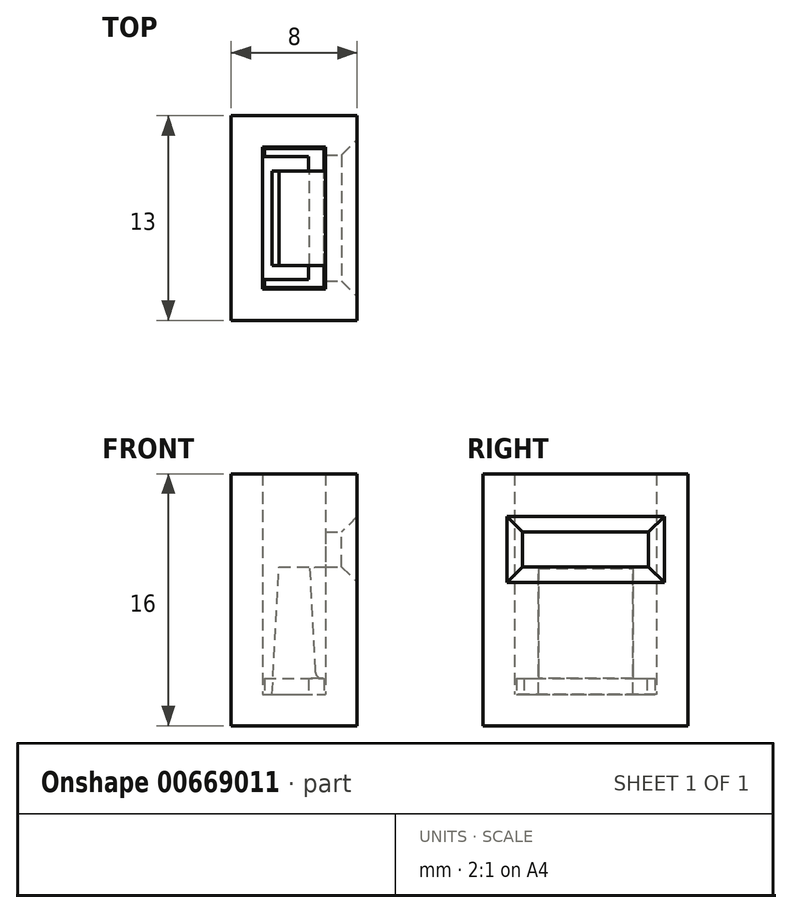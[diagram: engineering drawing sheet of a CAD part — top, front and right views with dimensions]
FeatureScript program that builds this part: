
annotation { "Feature Type Name" : "Feature", "Feature Type Description" : "" }
export const myFeature = defineFeature(function(context is Context, id is Id, definition is map)
    precondition{}
    {
        {
            var Q0;
            Q0=qCreatedBy(makeId("Top.planeOp"),FACE);
            var sketch = newSketch(context, id + "F0", { "sketchPlane" : qUnion([Q0])});
            skLineSegment(sketch, "E0.bottom", {"start": v(-2, 4.5) * mm, "end": v(2, 4.5) * mm});
            skLineSegment(sketch, "E0.top", {"start": v(-2, -4.5) * mm, "end": v(2, -4.5) * mm});
            skLineSegment(sketch, "E0.left", {"start": v(-2, 4.5) * mm, "end": v(-2, -4.5) * mm});
            skLineSegment(sketch, "E0.right", {"start": v(2, 4.5) * mm, "end": v(2, -4.5) * mm});
            skLineSegment(sketch, "E1.bottom", {"start": v(-4, 6.5) * mm, "end": v(4, 6.5) * mm});
            skLineSegment(sketch, "E1.top", {"start": v(-4, -6.5) * mm, "end": v(4, -6.5) * mm});
            skLineSegment(sketch, "E1.left", {"start": v(-4, 6.5) * mm, "end": v(-4, -6.5) * mm});
            skLineSegment(sketch, "E1.right", {"start": v(4, 6.5) * mm, "end": v(4, -6.5) * mm});
            skLineSegment(sketch, "E2", {"start": v(0, 4.5) * mm, "end": v(0, -4.5) * mm});
            skLineSegment(sketch, "E3", {"start": v(-2, 0) * mm, "end": v(2, 0) * mm});
            skSolve(sketch);
        }
        {
            var Q0;
            Q0=makeQuery(id+"F0.imprint","IMPRINT",FACE,{"disambiguationData":[TD([[makeQuery(id+"F0.imprint","IMPRINT",EDGE,{"derivedFrom":sQuery(id+"F0.wireOp",EDGE,"E1.bottom")}),-1.0]])]});
            extrude(context, id + "F1", {"entities" : qUnion([Q0]), "depth" : 14 * mm, "offsetDistance" : 25 * mm});
        }
        {
            var Q0;
            Q0=qCreatedBy(makeId("Front.planeOp"),FACE);
            var sketch = newSketch(context, id + "F2", { "sketchPlane" : qUnion([Q0])});
            skLineSegment(sketch, "E4", {"start": v(-1.4, 0) * mm, "end": v(1.4, 0) * mm});
            skLineSegment(sketch, "E5", {"start": v(-1.4, 0) * mm, "end": v(-0.88, 10) * mm});
            skLineSegment(sketch, "E6", {"start": v(-0.88, 10) * mm, "end": v(2.03, 10) * mm});
            skLineSegment(sketch, "E7", {"start": v(2.4, 8.62) * mm, "end": v(2.03, 10) * mm});
            skLineSegment(sketch, "E8", {"start": v(2.4, 8.62) * mm, "end": v(2.4, 8.12) * mm});
            skLineSegment(sketch, "E9", {"start": v(2.4, 8.12) * mm, "end": v(0.98, 8) * mm});
            skLineSegment(sketch, "E10", {"start": v(0.98, 8) * mm, "end": v(1.4, 0) * mm});
            skLineSegment(sketch, "E11", {"start": v(-1.4, 0) * mm, "end": v(-1.4, 10) * mm});
            skLineSegment(sketch, "E12", {"start": v(-1.4, 10) * mm, "end": v(-0.88, 10) * mm});
            skLineSegment(sketch, "E13", {"start": v(2.4, 8.12) * mm, "end": v(2.4, 0) * mm});
            skLineSegment(sketch, "E14", {"start": v(2.4, 0) * mm, "end": v(1.4, 0) * mm});
            skLineSegment(sketch, "E15", {"start": v(2.03, 10) * mm, "end": v(2.4, 10) * mm});
            skLineSegment(sketch, "E16", {"start": v(2.4, 10) * mm, "end": v(2.4, 8.62) * mm});
            skLineSegment(sketch, "E17.0", {"start": v(2, 14) * mm, "end": v(2, 0) * mm});
            skLineSegment(sketch, "E18.0", {"start": v(-2, 14) * mm, "end": v(-2, 0) * mm});
            skLineSegment(sketch, "E19.bottom", {"start": v(-1.5, 10.3) * mm, "end": v(5.4, 10.3) * mm});
            skLineSegment(sketch, "E19.top", {"start": v(-1.5, 8.1) * mm, "end": v(5.4, 8.1) * mm});
            skLineSegment(sketch, "E19.left", {"start": v(-1.5, 10.3) * mm, "end": v(-1.5, 8.1) * mm});
            skLineSegment(sketch, "E19.right", {"start": v(5.4, 10.3) * mm, "end": v(5.4, 8.1) * mm});
            skSolve(sketch);
        }
        {
            var Q0;
            Q0=makeQuery(id+"F1.opExtrude","CAP_FACE",FACE,{"disambiguationData":[OSD([sQuery(id+"F0.wireOp",EDGE,"E0.bottom"),sQuery(id+"F0.wireOp",EDGE,"E0.top"),sQuery(id+"F0.wireOp",EDGE,"E0.left"),sQuery(id+"F0.wireOp",EDGE,"E0.right"),sQuery(id+"F0.wireOp",EDGE,"E1.bottom"),sQuery(id+"F0.wireOp",EDGE,"E1.top"),sQuery(id+"F0.wireOp",EDGE,"E1.left"),sQuery(id+"F0.wireOp",EDGE,"E1.right")])],"isStart":true});
            var sketch = newSketch(context, id + "F3", { "sketchPlane" : qUnion([Q0])});
            skLineSegment(sketch, "E20.bottom", {"start": v(-1.9, 4.4) * mm, "end": v(1.9, 4.4) * mm});
            skLineSegment(sketch, "E20.top", {"start": v(-1.9, -4.4) * mm, "end": v(1.9, -4.4) * mm});
            skLineSegment(sketch, "E20.left", {"start": v(-1.9, 4.4) * mm, "end": v(-1.9, -4.4) * mm});
            skLineSegment(sketch, "E20.right", {"start": v(1.9, 4.4) * mm, "end": v(1.9, -4.4) * mm});
            skLineSegment(sketch, "E21.bottom", {"start": v(-4, 6.5) * mm, "end": v(4, 6.5) * mm});
            skLineSegment(sketch, "E21.top", {"start": v(-4, -6.5) * mm, "end": v(4, -6.5) * mm});
            skLineSegment(sketch, "E21.left", {"start": v(-4, 6.5) * mm, "end": v(-4, -6.5) * mm});
            skLineSegment(sketch, "E21.right", {"start": v(4, 6.5) * mm, "end": v(4, -6.5) * mm});
            skLineSegment(sketch, "E22.bottom", {"start": v(-1.9, 3.9) * mm, "end": v(0.9, 3.9) * mm});
            skLineSegment(sketch, "E22.top", {"start": v(-1.9, -3.9) * mm, "end": v(0.9, -3.9) * mm});
            skLineSegment(sketch, "E22.left", {"start": v(-1.9, 3.9) * mm, "end": v(-1.9, -3.9) * mm});
            skLineSegment(sketch, "E22.right", {"start": v(0.9, 3.9) * mm, "end": v(0.9, -3.9) * mm});
            skSolve(sketch);
        }
        {
            var Q0;
            Q0=makeQuery(id+"F3.imprint","IMPRINT",FACE,{"disambiguationData":[TD([[makeQuery(id+"F3.imprint","IMPRINT",EDGE,{"derivedFrom":sQuery(id+"F3.wireOp",EDGE,"E21.bottom")}),-1.0]])]});
            var Q1;
            Q1=makeQuery(id+"F3.imprint","IMPRINT",FACE,{"disambiguationData":[TD([[makeQuery(id+"F3.imprint","IMPRINT",EDGE,{"derivedFrom":sQuery(id+"F3.wireOp",EDGE,"E20.bottom")}),-1.0]])]});
            var Q2;
            Q2=makeQuery(id+"F3.imprint","IMPRINT",FACE,{"disambiguationData":[TD([[makeQuery(id+"F3.imprint","IMPRINT",EDGE,{"derivedFrom":sQuery(id+"F3.wireOp",EDGE,"E20.bottom")}),1.0]])]});
            var Q3;
            Q3=makeQuery(id+"F3.imprint","IMPRINT",FACE,{"disambiguationData":[TD([[makeQuery(id+"F3.imprint","IMPRINT",EDGE,{"derivedFrom":sQuery(id+"F3.wireOp",EDGE,"E22.bottom")}),-1.0]])]});
            extrude(context, id + "F4", {"entities" : qUnion([Q0, Q1, Q2, Q3]), "depth" : 2 * mm, "offsetDistance" : 25 * mm});
        }
        {
            var Q0;
            Q0=makeQuery(id+"F3.imprint","IMPRINT",FACE,{"disambiguationData":[TD([[makeQuery(id+"F3.imprint","IMPRINT",EDGE,{"derivedFrom":sQuery(id+"F3.wireOp",EDGE,"E20.bottom")}),-1.0]])]});
            extrude(context, id + "F5", {"entities" : qUnion([Q0]), "operationType" : NewBodyOperationType.ADD, "oppositeDirection" : true, "depth" : 1 * mm, "offsetDistance" : 25 * mm});
        }
        {
            var Q0;
            Q0=makeQuery(id+"F2.imprint","IMPRINT",FACE,{"disambiguationData":[TD([[makeQuery(id+"F2.imprint","IMPRINT",EDGE,{"derivedFrom":sQuery(id+"F2.wireOp",EDGE,"E4")}),1.0]])]});
            var Q1;
            {var subQ0=sQuery(id+"F2.wireOp",EDGE,"E8");Q1=makeQuery(id+"F2.imprint","IMPRINT",FACE,{"disambiguationData":[TD([[makeQuery(id+"F2.imprint","IMPRINT",EDGE,{"derivedFrom":subQ0}),-1.0]])]});}
            var Q2;
            {var subQ1=sQuery(id+"F2.wireOp",EDGE,"E6");Q2=makeQuery(id+"F2.imprint","IMPRINT",FACE,{"disambiguationData":[TD([[makeQuery(id+"F2.imprint","IMPRINT",EDGE,{"derivedFrom":subQ1}),-1.0]])]});}
            extrude(context, id + "F6", {"entities" : qUnion([Q0, Q1, Q2]), "operationType" : NewBodyOperationType.ADD, "depth" : 3 * mm, "offsetDistance" : 25 * mm, "hasSecondDirection" : true, "secondDirectionOppositeDirection" : true, "secondDirectionDepth" : 3 * mm});
        }
        {
            var Q0;
            Q0=makeQuery(id+"F6.opExtrude","SWEPT_EDGE",EDGE,{"disambiguationData":[OSD([sQuery(id+"F2.wireOp",EDGE,"E4"),sQuery(id+"F2.wireOp",EDGE,"E5"),sQuery(id+"F2.wireOp",EDGE,"E11")])]});
            var Q1;
            Q1=makeQuery(id+"F6.boolean.opBoolean","INTERSECT",EDGE,{"derivedFrom":[makeQuery(id+"F5.opExtrude","CAP_FACE",FACE,{"disambiguationData":[OSD([sQuery(id+"F3.wireOp",EDGE,"E20.bottom"),sQuery(id+"F3.wireOp",EDGE,"E20.top"),sQuery(id+"F3.wireOp",EDGE,"E20.left"),sQuery(id+"F3.wireOp",EDGE,"E20.right"),sQuery(id+"F3.wireOp",EDGE,"E22.bottom"),sQuery(id+"F3.wireOp",EDGE,"E22.top"),sQuery(id+"F3.wireOp",EDGE,"E22.right")])],"isStart":false}),makeQuery(id+"F6.opExtrude","SWEPT_FACE",FACE,{"disambiguationData":[OSD([sQuery(id+"F2.wireOp",EDGE,"E10")])]})]});
            fillet(context, id + "F7", {"entities" : qUnion([Q0, Q1]), "radius" : 0.5 * mm, "tangentPropagation" : true, "allowEdgeOverflow" : false});
        }
        {
            var Q0;
            {var subQ5=sQuery(id+"F2.wireOp",EDGE,"E8");Q0=makeQuery(id+"F2.imprint","IMPRINT",FACE,{"disambiguationData":[TD([[makeQuery(id+"F2.imprint","IMPRINT",EDGE,{"derivedFrom":subQ5}),1.0]])]});}
            var Q1;
            {var subQ6=sQuery(id+"F2.wireOp",EDGE,"E6");Q1=makeQuery(id+"F2.imprint","IMPRINT",FACE,{"disambiguationData":[TD([[makeQuery(id+"F2.imprint","IMPRINT",EDGE,{"derivedFrom":subQ6}),1.0]])]});}
            var Q2;
            {var subQ0=sQuery(id+"F2.wireOp",EDGE,"E12");Q2=makeQuery(id+"F2.imprint","IMPRINT",FACE,{"disambiguationData":[TD([[makeQuery(id+"F2.imprint","IMPRINT",EDGE,{"derivedFrom":subQ0}),-1.0]])]});}
            var Q3;
            {var subQ0=sQuery(id+"F2.wireOp",EDGE,"E16");Q3=makeQuery(id+"F2.imprint","IMPRINT",FACE,{"disambiguationData":[TD([[makeQuery(id+"F2.imprint","IMPRINT",EDGE,{"derivedFrom":subQ0}),-1.0]])]});}
            var Q4;
            {var subQ1=sQuery(id+"F2.wireOp",EDGE,"E6");Q4=makeQuery(id+"F2.imprint","IMPRINT",FACE,{"disambiguationData":[TD([[makeQuery(id+"F2.imprint","IMPRINT",EDGE,{"derivedFrom":subQ1}),-1.0]])]});}
            var Q5;
            {var subQ0=sQuery(id+"F2.wireOp",EDGE,"E8");Q5=makeQuery(id+"F2.imprint","IMPRINT",FACE,{"disambiguationData":[TD([[makeQuery(id+"F2.imprint","IMPRINT",EDGE,{"derivedFrom":subQ0}),-1.0]])]});}
            var Q6;
            {var subQ0=sQuery(id+"F2.wireOp",EDGE,"E6");var subQ5=sQuery(id+"F2.wireOp",EDGE,"E17.0");var subQ6=makeQuery(id+"F2.imprint","INTERSECT",VERTEX,{"derivedFrom":[subQ0,subQ5]});Q6=makeQuery(id+"F2.imprint","IMPRINT",FACE,{"disambiguationData":[TD([[makeQuery(id+"F2.imprint","IMPRINT",EDGE,{"disambiguationData":[TD([[subQ6,-1.0]])],"derivedFrom":subQ5}),-1.0]])]});}
            var Q7;
            {var subQ0=sQuery(id+"F2.wireOp",EDGE,"E13");var subQ3=sQuery(id+"F2.wireOp",EDGE,"E19.top");var subQ5=makeQuery(id+"F2.imprint","INTERSECT",VERTEX,{"derivedFrom":[subQ0,subQ3]});Q7=makeQuery(id+"F2.imprint","IMPRINT",FACE,{"disambiguationData":[TD([[makeQuery(id+"F2.imprint","IMPRINT",EDGE,{"disambiguationData":[TD([[subQ5,1.0]])],"derivedFrom":subQ3}),1.0]])]});}
            extrude(context, id + "F8", {"entities" : qUnion([Q0, Q1, Q2, Q3, Q4, Q5, Q6, Q7]), "operationType" : NewBodyOperationType.REMOVE, "oppositeDirection" : true, "depth" : 4 * mm, "offsetDistance" : 25 * mm, "hasSecondDirection" : true, "secondDirectionOppositeDirection" : false, "secondDirectionDepth" : 4 * mm});
        }
        {
            var Q0;
            Q0=makeQuery(id+"F8.boolean.opBoolean","INTERSECT",EDGE,{"derivedFrom":[makeQuery(id+"F1.opExtrude","SWEPT_FACE",FACE,{"disambiguationData":[OSD([sQuery(id+"F0.wireOp",EDGE,"E1.right")])]}),makeQuery(id+"F8.opExtrude","SWEPT_FACE",FACE,{"disambiguationData":[OSD([sQuery(id+"F2.wireOp",EDGE,"E19.bottom")])]})]});
            var Q1;
            Q1=makeQuery(id+"F8.boolean.opBoolean","INTERSECT",EDGE,{"derivedFrom":[makeQuery(id+"F1.opExtrude","SWEPT_FACE",FACE,{"disambiguationData":[OSD([sQuery(id+"F0.wireOp",EDGE,"E1.right")])]}),makeQuery(id+"F8.opExtrude","CAP_FACE",FACE,{"disambiguationData":[OSD([sQuery(id+"F2.wireOp",EDGE,"E19.bottom"),sQuery(id+"F2.wireOp",EDGE,"E19.top"),sQuery(id+"F2.wireOp",EDGE,"E19.left"),sQuery(id+"F2.wireOp",EDGE,"E19.right")])],"isStart":false})]});
            var Q2;
            Q2=makeQuery(id+"F8.boolean.opBoolean","INTERSECT",EDGE,{"derivedFrom":[makeQuery(id+"F1.opExtrude","SWEPT_FACE",FACE,{"disambiguationData":[OSD([sQuery(id+"F0.wireOp",EDGE,"E1.right")])]}),makeQuery(id+"F8.opExtrude","SWEPT_FACE",FACE,{"disambiguationData":[OSD([sQuery(id+"F2.wireOp",EDGE,"E19.top")])]})]});
            var Q3;
            Q3=makeQuery(id+"F8.boolean.opBoolean","INTERSECT",EDGE,{"derivedFrom":[makeQuery(id+"F1.opExtrude","SWEPT_FACE",FACE,{"disambiguationData":[OSD([sQuery(id+"F0.wireOp",EDGE,"E1.right")])]}),makeQuery(id+"F8.opExtrude","CAP_FACE",FACE,{"disambiguationData":[OSD([sQuery(id+"F2.wireOp",EDGE,"E19.bottom"),sQuery(id+"F2.wireOp",EDGE,"E19.top"),sQuery(id+"F2.wireOp",EDGE,"E19.left"),sQuery(id+"F2.wireOp",EDGE,"E19.right")])],"isStart":true})]});
            chamfer(context, id + "F9", {"entities" : qUnion([Q0, Q1, Q2, Q3]), "width" : 1 * mm, "tangentPropagation" : true});
        }
    });
